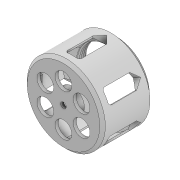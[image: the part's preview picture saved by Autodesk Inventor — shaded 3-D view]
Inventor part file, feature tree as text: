
AUTODESK INVENTOR PART (.ipt)
format: ipt  version: 2020 (Build 240168000, 168)  size: 507,904 bytes
history: native  units: mm
features: sketch x9, extrude x8, chamfer x5, pattern_circular x2, helix x1, fillet x1, thicken_offset x1
ambient origin geometry x8: Origin, YZ Plane, XZ Plane, XY Plane, X Axis, Y Axis, Z Axis, Center Point
bodies: Solid1 (feature_tree)
feature tree (27):
  extrude  "Extrusion1"  Depth=7.0mm
  helix  "Coil1"  [1 undecoded]
  chamfer  "Chamfer1"  Distance=0.475mm Angle=45.0deg
  extrude  "Extrusion2"  Depth=36.0mm
  chamfer  "Chamfer2"  Distance=3.0mm
  extrude  "Extrusion3"  Depth=1.2mm
  extrude  "Extrusion4"  Depth=5.0mm
  chamfer  "Chamfer3"  Distance=12.0mm
  extrude  "Extrusion5"  Depth=5.0mm TaperAngle=360.0deg
  chamfer  "Chamfer4"  Distance=1.2mm
  extrude  "Extrusion6"  Depth=5.0mm TaperAngle=45.0deg
  chamfer  "Chamfer5"  Distance=16.0mm
  fillet  "Fillet1"  Radius=0.8mm
  pattern_circular  "Circular Pattern1"  [2 undecoded]
  extrude  "Extrusion7"  Depth=5.0mm TaperAngle=45.0deg
  thicken_offset  "Thicken1"
  extrude  "Extrusion8"  Depth=10.0mm
  pattern_circular  "Circular Pattern2"  [2 undecoded]
  sketch  "Sketch1"  dims[d0=43.9mm d1=1.6mm d2=7.0mm d3=0.0mm]
  sketch  "Sketch2"  dims[d4=1.2mm]
  sketch  "Sketch3"  dims[d5=0.8mm]
  sketch  "Sketch4"  dims[d6=1.5mm]
  sketch  "Sketch5"  dims[d7=5.8mm d8=10.0mm d9=0.0mm d10=90.0deg d11=90.0deg d12=0.0mm d13=0.0mm d14=0.475mm d15=2.0mm d16=45.0deg]
  sketch  "Sketch6"  dims[d17=56.0mm d18=36.0mm]
  sketch  "Sketch7"  dims[d19=1.2mm d20=3.0mm d21=0.0mm]
  sketch  "Sketch8"  dims[d22=1.45mm d23=2.0mm d24=45.0deg d25=1.2mm]
  sketch  "Sketch9"  dims[d26=30.0mm d27=0.0mm d28=15.0mm d29=12.0mm d30=60.0mm d32=360.0deg d34=1.2mm d35=0.0mm d36=4.85mm d37=2.0mm d38=45.0deg d39=16.0mm d40=0.8mm d41=4.0mm d42=0.0mm d43=1.0mm d44=2.0mm d45=45.0deg d46=10.0mm d47=10.0mm d48=0.0mm d49=5.0mm d50=2.0mm d51=45.0deg d52=2.0mm d53=60.0mm d54=360.0deg d56=4.0mm d57=10.0mm d58=0.0mm d59=1.0mm d60=1.0mm d61=3.0mm d62=2.96706mm d63=0.523599mm d64=1.2mm d65=5.0mm d66=0.0mm d67=30.0mm d68=360.0deg]
note: 5 required parameter values undecoded (feature->parameter linkage not recoverable at this tier; creation-order binding heuristic only, values carry confidence <= 0.55)
